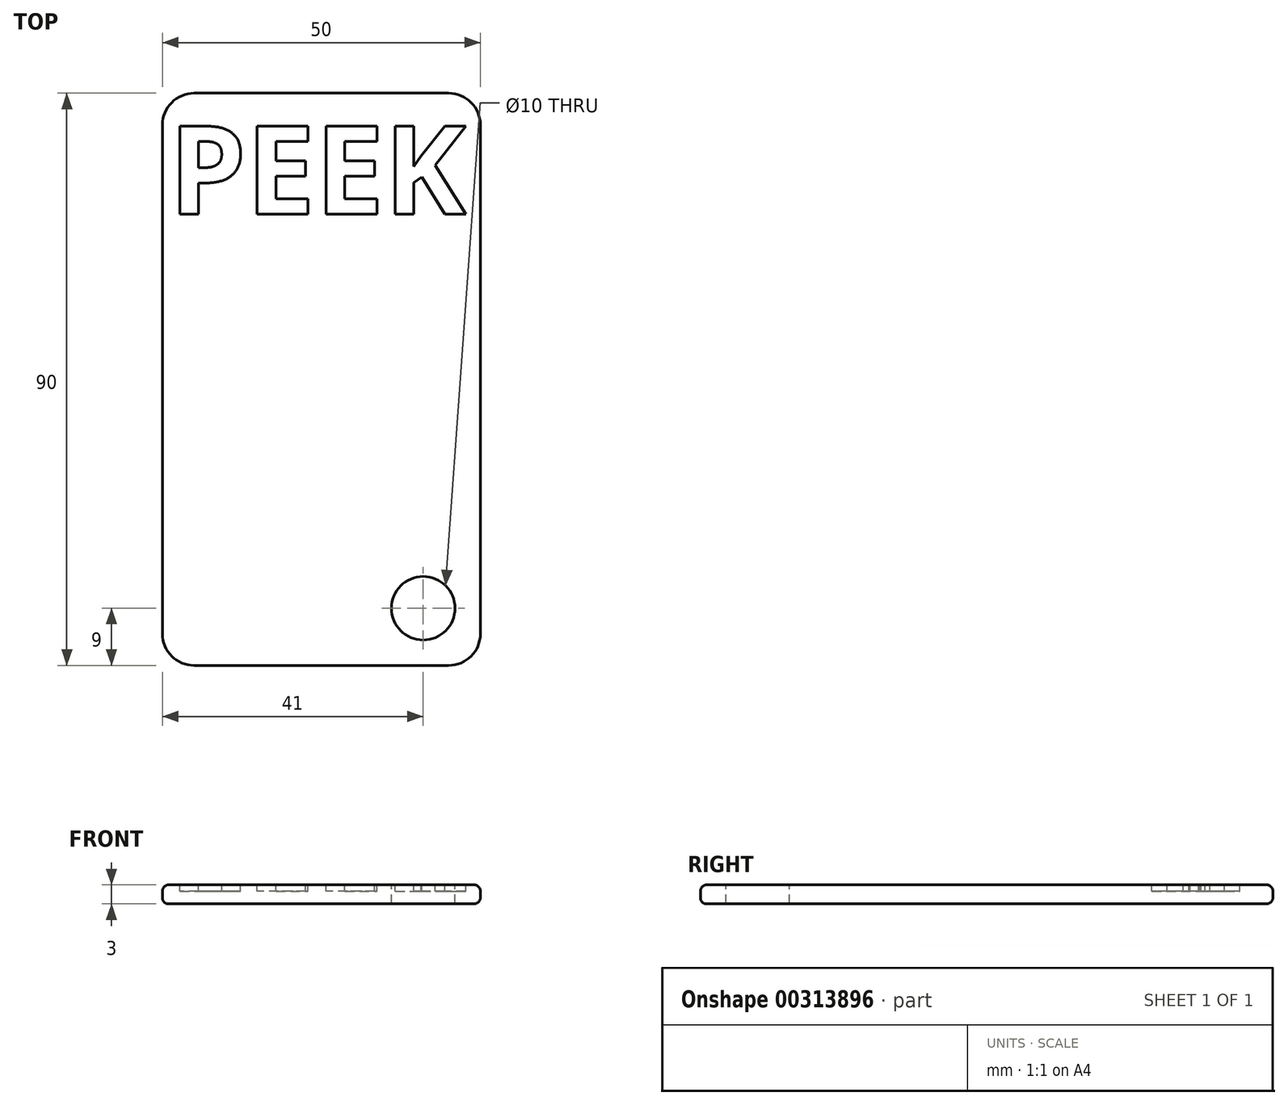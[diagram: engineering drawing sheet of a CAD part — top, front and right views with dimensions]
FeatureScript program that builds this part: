
annotation { "Feature Type Name" : "Feature", "Feature Type Description" : "" }
export const myFeature = defineFeature(function(context is Context, id is Id, definition is map)
    precondition{}
    {
        {
            var Q0;
            Q0=qCreatedBy(makeId("Top.planeOp"),FACE);
            var sketch = newSketch(context, id + "F0", { "sketchPlane" : qUnion([Q0])});
            skLineSegment(sketch, "E0.bottom", {"start": v(-45, 25) * mm, "end": v(45, 25) * mm});
            skLineSegment(sketch, "E0.top", {"start": v(-45, -25) * mm, "end": v(45, -25) * mm});
            skLineSegment(sketch, "E0.left", {"start": v(-45, 25) * mm, "end": v(-45, -25) * mm});
            skLineSegment(sketch, "E0.right", {"start": v(45, 25) * mm, "end": v(45, -25) * mm});
            skLineSegment(sketch, "E1", {"start": v(-45, 25) * mm, "end": v(45, -25) * mm, "construction": true});
            skSolve(sketch);
        }
        {
            var Q0;
            Q0=makeQuery(id+"F0.imprint","IMPRINT",FACE,{"disambiguationData":[TD([[makeQuery(id+"F0.imprint","IMPRINT",EDGE,{"derivedFrom":sQuery(id+"F0.wireOp",EDGE,"E0.bottom")}),-1.0]])]});
            extrude(context, id + "F1", {"entities" : qUnion([Q0]), "depth" : 3 * mm});
        }
        {
            var Q0;
            Q0=makeQuery(id+"F1.opExtrude","CAP_FACE",FACE,{"disambiguationData":[OSD([sQuery(id+"F0.wireOp",EDGE,"E0.bottom"),sQuery(id+"F0.wireOp",EDGE,"E0.top"),sQuery(id+"F0.wireOp",EDGE,"E0.left"),sQuery(id+"F0.wireOp",EDGE,"E0.right")])],"isStart":false});
            var Q1;
            Q1=makeQuery(id+"F1.opExtrude","CAP_FACE",FACE,{"disambiguationData":[OSD([sQuery(id+"F0.wireOp",EDGE,"E0.bottom"),sQuery(id+"F0.wireOp",EDGE,"E0.top"),sQuery(id+"F0.wireOp",EDGE,"E0.left"),sQuery(id+"F0.wireOp",EDGE,"E0.right")])],"isStart":true});
            fillet(context, id + "F2", {"entities" : qUnion([Q0, Q1]), "radius" : 1 * mm, "tangentPropagation" : true, "allowEdgeOverflow" : false});
        }
        {
            var Q0;
            Q0=makeQuery(id+"F1.opExtrude","SWEPT_EDGE",EDGE,{"disambiguationData":[OSD([sQuery(id+"F0.wireOp",EDGE,"E0.top"),sQuery(id+"F0.wireOp",EDGE,"E0.right")])]});
            var Q1;
            Q1=makeQuery(id+"F1.opExtrude","SWEPT_EDGE",EDGE,{"disambiguationData":[OSD([sQuery(id+"F0.wireOp",EDGE,"E0.bottom"),sQuery(id+"F0.wireOp",EDGE,"E0.right")])]});
            var Q2;
            Q2=makeQuery(id+"F1.opExtrude","SWEPT_EDGE",EDGE,{"disambiguationData":[OSD([sQuery(id+"F0.wireOp",EDGE,"E0.bottom"),sQuery(id+"F0.wireOp",EDGE,"E0.left")])]});
            var Q3;
            Q3=makeQuery(id+"F1.opExtrude","SWEPT_EDGE",EDGE,{"disambiguationData":[OSD([sQuery(id+"F0.wireOp",EDGE,"E0.top"),sQuery(id+"F0.wireOp",EDGE,"E0.left")])]});
            fillet(context, id + "F3", {"entities" : qUnion([Q0, Q1, Q2, Q3]), "radius" : 5 * mm, "tangentPropagation" : true, "allowEdgeOverflow" : false});
        }
        {
            var Q0;
            Q0=qCreatedBy(makeId("Right.planeOp"),FACE);
            var sketch = newSketch(context, id + "F4", { "sketchPlane" : qUnion([Q0])});
            skLineSegment(sketch, "E2", {"start": v(0, 0) * mm, "end": v(0, 32.9) * mm});
            skSolve(sketch);
        }
        {
            var Q0;
            Q0=makeQuery(id+"F1.opExtrude","SWEPT_BODY",BODY,{"disambiguationData":[OSD([sQuery(id+"F0.wireOp",EDGE,"E0.bottom"),sQuery(id+"F0.wireOp",EDGE,"E0.top"),sQuery(id+"F0.wireOp",EDGE,"E0.left"),sQuery(id+"F0.wireOp",EDGE,"E0.right")])]});
            var Q1;
            Q1=sQuery(id+"F4.wireOp",EDGE,"E2");
            transform(context, id + "F5", {"entities" : qUnion([Q0]), "transformType" : TransformType.ROTATION, "transformAxis" : qUnion([Q1]), "angle" : 90 * degree, "makeCopy" : false});
        }
        {
            var Q0;
            Q0=makeQuery(id+"F1.opExtrude","CAP_FACE",FACE,{"disambiguationData":[OSD([sQuery(id+"F0.wireOp",EDGE,"E0.bottom"),sQuery(id+"F0.wireOp",EDGE,"E0.top"),sQuery(id+"F0.wireOp",EDGE,"E0.left"),sQuery(id+"F0.wireOp",EDGE,"E0.right")])],"isStart":false});
            var sketch = newSketch(context, id + "F6", { "sketchPlane" : qUnion([Q0])});
            skText(sketch, "E3", { "text": "PEEK", "fontName": "OpenSans-Bold.ttf"});
            const initialGuessF6  = {"E3": [-0.024, 0.02597, 1, 0, 0.01395]};
            skSetInitialGuess(sketch, initialGuessF6);
            skSolve(sketch);
        }
        {
            var Q0;
            Q0=qSketchRegion(id+"F6",true);
            extrude(context, id + "F7", {"entities" : qUnion([Q0]), "operationType" : NewBodyOperationType.REMOVE, "oppositeDirection" : true, "depth" : 1 * mm});
        }
        {
            var Q0;
            {var subQ0=sQuery(id+"F0.wireOp",EDGE,"E0.left");var subQ2=sQuery(id+"F0.wireOp",EDGE,"E0.bottom");var subQ4=sQuery(id+"F0.wireOp",EDGE,"E0.right");var subQ6=sQuery(id+"F0.wireOp",EDGE,"E0.top");Q0=makeQuery(id+"F7.boolean.opBoolean","SPLIT",FACE,{"disambiguationData":[TD([makeQuery(id+"F7.opExtrude","SWEPT_FACE",FACE,{"disambiguationData":[OSD([sQuery(id+"F6.wireOp",EDGE,"E3.sketch_text.stroke-0")])]})])],"derivedFrom":makeQuery(id+"F1.opExtrude","CAP_FACE",FACE,{"disambiguationData":[OSD([subQ2,subQ6,subQ0,subQ4])],"isStart":false})});}
            var sketch = newSketch(context, id + "F8", { "sketchPlane" : qUnion([Q0])});
            skCircle(sketch, "E4", {"center": v(16, -36) * mm, "radius": 5 * mm});
            skSolve(sketch);
        }
        {
            var Q0;
            Q0=qSketchRegion(id+"F8",true);
            extrude(context, id + "F9", {"entities" : qUnion([Q0]), "operationType" : NewBodyOperationType.REMOVE, "oppositeDirection" : true, "depth" : 3 * mm});
        }
    });
